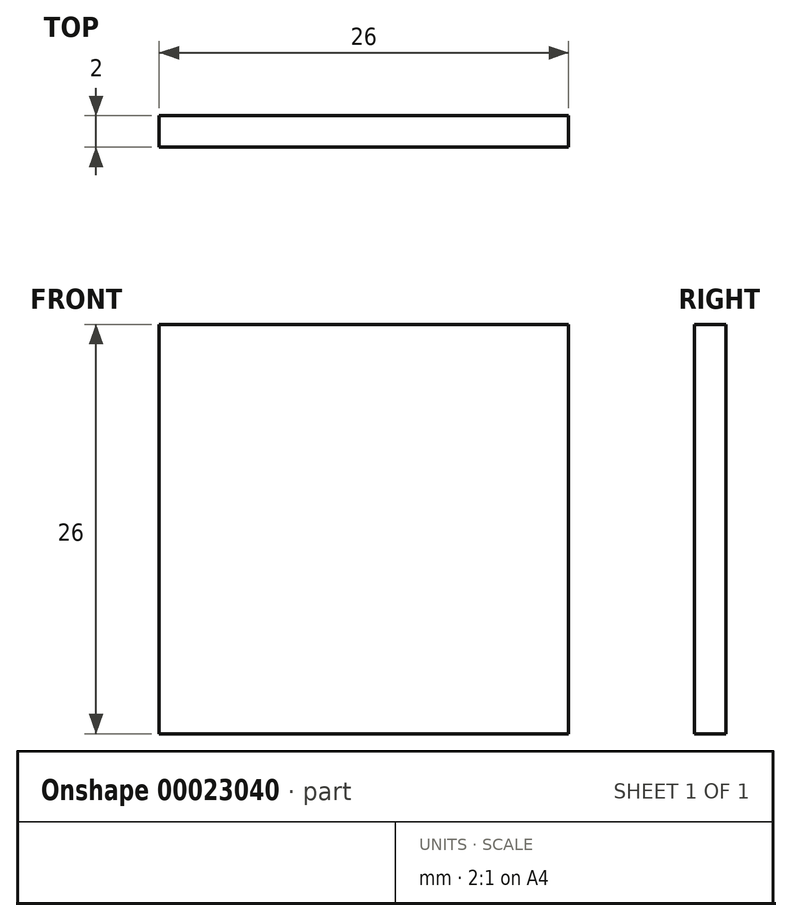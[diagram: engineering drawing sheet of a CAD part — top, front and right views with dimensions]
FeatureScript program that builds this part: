
annotation { "Feature Type Name" : "Feature", "Feature Type Description" : "" }
export const myFeature = defineFeature(function(context is Context, id is Id, definition is map)
    precondition{}
    {
        {
            var Q0;
            Q0=qCreatedBy(makeId("Front.planeOp"),FACE);
            var sketch = newSketch(context, id + "F0", { "sketchPlane" : qUnion([Q0])});
            skLineSegment(sketch, "E0.rect.bottom", {"start": v(13, 13) * mm, "end": v(-13, 13) * mm});
            skLineSegment(sketch, "E0.rect.top", {"start": v(13, -13) * mm, "end": v(-13, -13) * mm});
            skLineSegment(sketch, "E0.rect.left", {"start": v(13, 13) * mm, "end": v(13, -13) * mm});
            skLineSegment(sketch, "E0.rect.right", {"start": v(-13, 13) * mm, "end": v(-13, -13) * mm});
            skPoint(sketch, "E0.rect.middle", {"position": v(0, 0) * mm});
            skSolve(sketch);
        }
        {
            var Q0;
            Q0 = qSketchRegion(id + "F0", true);
            extrude(context, id + "F1", {"entities" : qUnion([Q0]), "depth" : 2 * mm});
        }
    });
